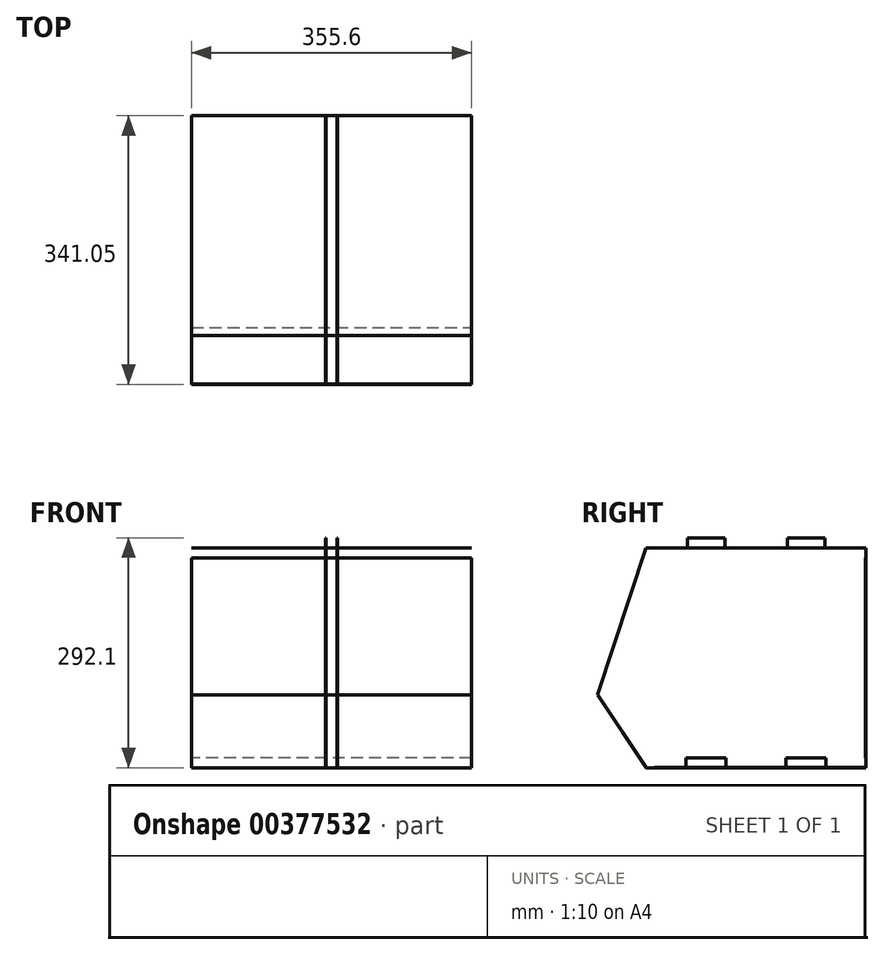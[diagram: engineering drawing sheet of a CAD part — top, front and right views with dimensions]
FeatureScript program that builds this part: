
annotation { "Feature Type Name" : "Feature", "Feature Type Description" : "" }
export const myFeature = defineFeature(function(context is Context, id is Id, definition is map)
    precondition{}
    {
        {
            assignVariable(context, id + "F0", {"name" : "thickness", "anyValue" : .5});
        }
        {
            assignVariable(context, id + "F1", {"name" : "width", "anyValue" : 14});
        }
        {
            var Q0;
            Q0=qCreatedBy(makeId("Right.planeOp"),FACE);
            var sketch = newSketch(context, id + "F2", { "sketchPlane" : qUnion([Q0])});
            skLineSegment(sketch, "E0", {"start": v(139.7, 139.7) * mm, "end": v(139.7, -139.7) * mm});
            skLineSegment(sketch, "E1", {"start": v(-139.7, -139.7) * mm, "end": v(-201.35, -47.25) * mm});
            skLineSegment(sketch, "E2", {"start": v(-201.35, -47.25) * mm, "end": v(-139.7, 139.7) * mm});
            skLineSegment(sketch, "E3", {"start": v(-139.7, -139.7) * mm, "end": v(-154.96, -139.7) * mm, "construction": true});
            skLineSegment(sketch, "E4", {"start": v(-154.96, -139.7) * mm, "end": v(-211.92, -54.3) * mm, "construction": true});
            skLineSegment(sketch, "E5", {"start": v(-211.92, -54.3) * mm, "end": v(-201.35, -47.25) * mm, "construction": true});
            skLineSegment(sketch, "E6", {"start": v(87.31, 139.7) * mm, "end": v(87.31, 152.4) * mm});
            skLineSegment(sketch, "E7", {"start": v(87.31, 152.4) * mm, "end": v(39.69, 152.4) * mm});
            skLineSegment(sketch, "E8", {"start": v(39.69, 152.4) * mm, "end": v(39.69, 139.7) * mm});
            skLineSegment(sketch, "E9", {"start": v(139.7, 139.7) * mm, "end": v(87.31, 139.7) * mm});
            skLineSegment(sketch, "E10", {"start": v(39.69, 139.7) * mm, "end": v(0, 139.7) * mm});
            skLineSegment(sketch, "E11", {"start": v(0, -139.7) * mm, "end": v(38.1, -139.7) * mm});
            skLineSegment(sketch, "E12", {"start": v(88.9, -127) * mm, "end": v(38.1, -127) * mm});
            skLineSegment(sketch, "E13", {"start": v(38.1, -127) * mm, "end": v(38.1, -139.7) * mm});
            skLineSegment(sketch, "E14", {"start": v(88.9, -127) * mm, "end": v(88.9, -139.7) * mm});
            skLineSegment(sketch, "E15", {"start": v(88.9, -139.7) * mm, "end": v(139.7, -139.7) * mm});
            skLineSegment(sketch, "E16.MirrorCS", {"start": v(-88.9, -139.7) * mm, "end": v(-139.7, -139.7) * mm});
            skLineSegment(sketch, "E17.MirrorCS", {"start": v(-88.9, -127) * mm, "end": v(-88.9, -139.7) * mm});
            skLineSegment(sketch, "E18.MirrorCS", {"start": v(-88.9, -127) * mm, "end": v(-38.1, -127) * mm});
            skLineSegment(sketch, "E19.MirrorCS", {"start": v(-38.1, -127) * mm, "end": v(-38.1, -139.7) * mm});
            skLineSegment(sketch, "E20.MirrorCS", {"start": v(0, -139.7) * mm, "end": v(-38.1, -139.7) * mm});
            skLineSegment(sketch, "E21.MirrorCS", {"start": v(-39.69, 152.4) * mm, "end": v(-39.69, 139.7) * mm});
            skLineSegment(sketch, "E22.MirrorCS", {"start": v(-87.31, 139.7) * mm, "end": v(-87.31, 152.4) * mm});
            skLineSegment(sketch, "E23.MirrorCS", {"start": v(-139.7, 139.7) * mm, "end": v(-87.31, 139.7) * mm});
            skLineSegment(sketch, "E24.MirrorCS", {"start": v(-87.31, 152.4) * mm, "end": v(-39.69, 152.4) * mm});
            skLineSegment(sketch, "E25.MirrorCS", {"start": v(-39.69, 139.7) * mm, "end": v(0, 139.7) * mm});
            skSolve(sketch);
        }
        {
            var Q0;
            Q0 = qSketchRegion(id + "F2", true);
            extrude(context, id + "F3", {"entities" : qUnion([Q0]), "depth" : (getVariable(context, 'width') / 2 + getVariable(context, 'thickness')) * mm, "hasSecondDirection" : true, "secondDirectionOppositeDirection" : false, "secondDirectionDepth" : (getVariable(context, 'width') / 2) * mm});
        }
        {
            var Q0;
            Q0=makeQuery(id+"F3.opExtrude","SWEPT_BODY",BODY,{"disambiguationData":[OSD([sQuery(id+"F2.wireOp",EDGE,"E0"),sQuery(id+"F2.wireOp",EDGE,"uS7o3Ql0-Hwbm-FKSR-uhZp-ccV8yQ46O6f3"),sQuery(id+"F2.wireOp",EDGE,"E1"),sQuery(id+"F2.wireOp",EDGE,"E2"),sQuery(id+"F2.wireOp",EDGE,"c3iYRHqb-eUdC-9xOQ-NnuV-AFuO0mQXi6aF")])]});
            var Q1;
            Q1=qCreatedBy(makeId("Right.planeOp"),FACE);
            mirror(context, id + "F4", {"entities" : qUnion([Q0]), "mirrorPlane" : qUnion([Q1])});
        }
        {
            var Q0;
            Q0=makeQuery(id+"F3.opExtrude","SWEPT_FACE",FACE,{"disambiguationData":[OSD([sQuery(id+"F2.wireOp",EDGE,"E9")])]});
            var sketch = newSketch(context, id + "F5", { "sketchPlane" : qUnion([Q0])});
            skPoint(sketch, "E26.0", {"position": v(-177.8, 139.7) * mm});
            skPoint(sketch, "E27.0", {"position": v(177.8, -139.7) * mm});
            skLineSegment(sketch, "E28.bottom", {"start": v(-177.8, 139.7) * mm, "end": v(177.8, 139.7) * mm});
            skLineSegment(sketch, "E28.top", {"start": v(-177.8, -139.7) * mm, "end": v(177.8, -139.7) * mm});
            skLineSegment(sketch, "E28.left", {"start": v(-177.8, 139.7) * mm, "end": v(-177.8, -139.7) * mm});
            skLineSegment(sketch, "E28.right", {"start": v(177.8, 139.7) * mm, "end": v(177.8, -139.7) * mm});
            skSolve(sketch);
        }
        {
            var Q0;
            Q0 = qSketchRegion(id + "F5", true);
            extrude(context, id + "F6", {"entities" : qUnion([Q0]), "oppositeDirection" : true, "depth" : (getVariable(context, 'thickness')) * mm});
        }
        {
            var Q0;
            Q0=makeQuery(id+"F4.opPattern","COPY",FACE,{"derivedFrom":makeQuery(id+"F3.opExtrude","SWEPT_FACE",FACE,{"disambiguationData":[OSD([sQuery(id+"F2.wireOp",EDGE,"E1")])]}),"instanceName":"1"});
            var sketch = newSketch(context, id + "F7", { "sketchPlane" : qUnion([Q0])});
            skPoint(sketch, "E29.0", {"position": v(-177.8, 72.4) * mm});
            skPoint(sketch, "E30.0", {"position": v(177.8, -38.72) * mm});
            skLineSegment(sketch, "E31.bottom", {"start": v(-177.8, 72.4) * mm, "end": v(177.8, 72.4) * mm});
            skLineSegment(sketch, "E31.top", {"start": v(-177.8, -38.72) * mm, "end": v(177.8, -38.72) * mm});
            skLineSegment(sketch, "E31.left", {"start": v(-177.8, 72.4) * mm, "end": v(-177.8, -38.72) * mm});
            skLineSegment(sketch, "E31.right", {"start": v(177.8, 72.4) * mm, "end": v(177.8, -38.72) * mm});
            skSolve(sketch);
        }
        {
            var Q0;
            Q0=makeQuery(id+"F7.imprint","IMPRINT",FACE,{"disambiguationData":[TD([[makeQuery(id+"F7.imprint","IMPRINT",EDGE,{"derivedFrom":sQuery(id+"F7.wireOp",EDGE,"E31.bottom")}),-1.0]])]});
            extrude(context, id + "F8", {"entities" : qUnion([Q0]), "oppositeDirection" : true, "depth" : (getVariable(context, 'thickness')) * mm});
        }
        {
            var Q0;
            Q0=makeQuery(id+"F3.opExtrude","SWEPT_FACE",FACE,{"disambiguationData":[OSD([sQuery(id+"F2.wireOp",EDGE,"E15")])]});
            var sketch = newSketch(context, id + "F9", { "sketchPlane" : qUnion([Q0])});
            skPoint(sketch, "E32.0", {"position": v(177.8, -139.7) * mm});
            skPoint(sketch, "E33.0", {"position": v(-177.8, 129.13) * mm});
            skLineSegment(sketch, "E34.bottom", {"start": v(-177.8, 129.13) * mm, "end": v(177.8, 129.13) * mm});
            skLineSegment(sketch, "E34.top", {"start": v(-177.8, -139.7) * mm, "end": v(177.8, -139.7) * mm});
            skLineSegment(sketch, "E34.left", {"start": v(-177.8, 129.13) * mm, "end": v(-177.8, -139.7) * mm});
            skLineSegment(sketch, "E34.right", {"start": v(177.8, 129.13) * mm, "end": v(177.8, -139.7) * mm});
            skSolve(sketch);
        }
        {
            var Q0;
            Q0 = qSketchRegion(id + "F9", true);
            extrude(context, id + "F10", {"entities" : qUnion([Q0]), "oppositeDirection" : true, "depth" : (getVariable(context, 'thickness')) * mm});
        }
        {
            var Q0;
            Q0=makeQuery(id+"F3.opExtrude","SWEPT_FACE",FACE,{"disambiguationData":[OSD([sQuery(id+"F2.wireOp",EDGE,"E0")])]});
            var sketch = newSketch(context, id + "F11", { "sketchPlane" : qUnion([Q0])});
            skPoint(sketch, "E35.0", {"position": v(-177.8, 127) * mm});
            skPoint(sketch, "E36.0", {"position": v(177.8, -127) * mm});
            skLineSegment(sketch, "E37.bottom", {"start": v(-177.8, 127) * mm, "end": v(177.8, 127) * mm});
            skLineSegment(sketch, "E37.top", {"start": v(-177.8, -127) * mm, "end": v(177.8, -127) * mm});
            skLineSegment(sketch, "E37.left", {"start": v(-177.8, 127) * mm, "end": v(-177.8, -127) * mm});
            skLineSegment(sketch, "E37.right", {"start": v(177.8, 127) * mm, "end": v(177.8, -127) * mm});
            skSolve(sketch);
        }
        {
            var Q0;
            Q0 = qSketchRegion(id + "F11", true);
            extrude(context, id + "F12", {"entities" : qUnion([Q0]), "oppositeDirection" : true, "depth" : (getVariable(context, 'thickness')) * mm});
        }
    });
